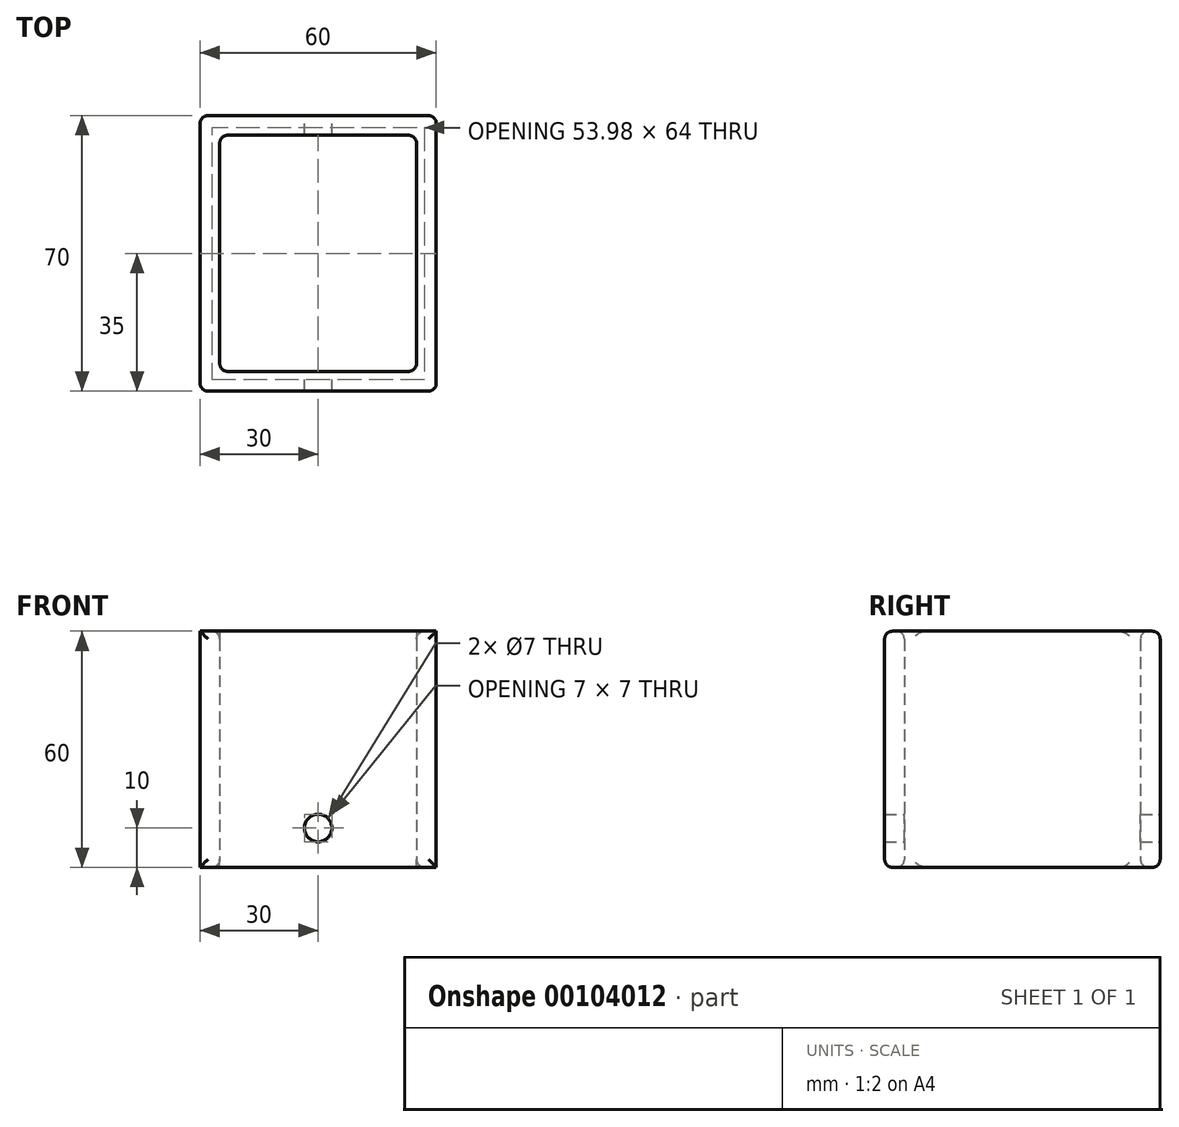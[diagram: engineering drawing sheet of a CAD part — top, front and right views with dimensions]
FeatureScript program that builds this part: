
annotation { "Feature Type Name" : "Feature", "Feature Type Description" : "" }
export const myFeature = defineFeature(function(context is Context, id is Id, definition is map)
    precondition{}
    {
        {
            var Q0;
            Q0=qCreatedBy(makeId("Top.planeOp"),FACE);
            var sketch = newSketch(context, id + "F0", { "sketchPlane" : qUnion([Q0])});
            skLineSegment(sketch, "E0.bottom", {"start": v(-30, 35) * mm, "end": v(30, 35) * mm});
            skLineSegment(sketch, "E0.top", {"start": v(-30, -35) * mm, "end": v(30, -35) * mm});
            skLineSegment(sketch, "E0.left", {"start": v(-30, 35) * mm, "end": v(-30, -35) * mm});
            skLineSegment(sketch, "E0.right", {"start": v(30, 35) * mm, "end": v(30, -35) * mm});
            skPoint(sketch, "E0.middle", {"position": v(0, 0) * mm});
            skLineSegment(sketch, "E1.bottom", {"start": v(25, 30) * mm, "end": v(-25, 30) * mm});
            skLineSegment(sketch, "E1.top", {"start": v(25, -30) * mm, "end": v(-25, -30) * mm});
            skLineSegment(sketch, "E1.left", {"start": v(25, 30) * mm, "end": v(25, -30) * mm});
            skLineSegment(sketch, "E1.right", {"start": v(-25, 30) * mm, "end": v(-25, -30) * mm});
            skSolve(sketch);
        }
        {
            var Q0;
            Q0=makeQuery(id+"F0.imprint","IMPRINT",FACE,{"disambiguationData":[TD([[makeQuery(id+"F0.imprint","IMPRINT",EDGE,{"derivedFrom":sQuery(id+"F0.wireOp",EDGE,"E0.bottom")}),-1.0]])]});
            extrude(context, id + "F1", {"entities" : qUnion([Q0]), "depth" : 60 * mm});
        }
        {
            var Q0;
            Q0=makeQuery(id+"F1.opExtrude","SWEPT_EDGE",EDGE,{"disambiguationData":[OSD([sQuery(id+"F0.wireOp",EDGE,"E0.bottom"),sQuery(id+"F0.wireOp",EDGE,"E0.left")])]});
            var Q1;
            Q1=makeQuery(id+"F1.opExtrude","CAP_EDGE",EDGE,{"disambiguationData":[OSD([sQuery(id+"F0.wireOp",EDGE,"E0.bottom")])],"isStart":false});
            var Q2;
            Q2=makeQuery(id+"F1.opExtrude","SWEPT_EDGE",EDGE,{"disambiguationData":[OSD([sQuery(id+"F0.wireOp",EDGE,"E0.bottom"),sQuery(id+"F0.wireOp",EDGE,"E0.right")])]});
            var Q3;
            Q3=makeQuery(id+"F1.opExtrude","CAP_EDGE",EDGE,{"disambiguationData":[OSD([sQuery(id+"F0.wireOp",EDGE,"E0.bottom")])],"isStart":true});
            var Q4;
            Q4=makeQuery(id+"F1.opExtrude","SWEPT_EDGE",EDGE,{"disambiguationData":[OSD([sQuery(id+"F0.wireOp",EDGE,"E0.top"),sQuery(id+"F0.wireOp",EDGE,"E0.right")])]});
            var Q5;
            Q5=makeQuery(id+"F1.opExtrude","CAP_EDGE",EDGE,{"disambiguationData":[OSD([sQuery(id+"F0.wireOp",EDGE,"E0.top")])],"isStart":false});
            var Q6;
            Q6=makeQuery(id+"F1.opExtrude","SWEPT_EDGE",EDGE,{"disambiguationData":[OSD([sQuery(id+"F0.wireOp",EDGE,"E0.top"),sQuery(id+"F0.wireOp",EDGE,"E0.left")])]});
            var Q7;
            Q7=makeQuery(id+"F1.opExtrude","CAP_EDGE",EDGE,{"disambiguationData":[OSD([sQuery(id+"F0.wireOp",EDGE,"E0.top")])],"isStart":true});
            var Q8;
            Q8=makeQuery(id+"F1.opExtrude","SWEPT_EDGE",EDGE,{"disambiguationData":[OSD([sQuery(id+"F0.wireOp",EDGE,"E1.top"),sQuery(id+"F0.wireOp",EDGE,"E1.right")])]});
            var Q9;
            Q9=makeQuery(id+"F1.opExtrude","CAP_EDGE",EDGE,{"disambiguationData":[OSD([sQuery(id+"F0.wireOp",EDGE,"E1.top")])],"isStart":false});
            var Q10;
            Q10=makeQuery(id+"F1.opExtrude","SWEPT_EDGE",EDGE,{"disambiguationData":[OSD([sQuery(id+"F0.wireOp",EDGE,"E1.top"),sQuery(id+"F0.wireOp",EDGE,"E1.left")])]});
            var Q11;
            Q11=makeQuery(id+"F1.opExtrude","CAP_EDGE",EDGE,{"disambiguationData":[OSD([sQuery(id+"F0.wireOp",EDGE,"E1.top")])],"isStart":true});
            var Q12;
            Q12=makeQuery(id+"F1.opExtrude","SWEPT_EDGE",EDGE,{"disambiguationData":[OSD([sQuery(id+"F0.wireOp",EDGE,"E1.bottom"),sQuery(id+"F0.wireOp",EDGE,"E1.left")])]});
            var Q13;
            Q13=makeQuery(id+"F1.opExtrude","CAP_EDGE",EDGE,{"disambiguationData":[OSD([sQuery(id+"F0.wireOp",EDGE,"E1.bottom")])],"isStart":false});
            var Q14;
            Q14=makeQuery(id+"F1.opExtrude","CAP_EDGE",EDGE,{"disambiguationData":[OSD([sQuery(id+"F0.wireOp",EDGE,"E1.bottom")])],"isStart":true});
            var Q15;
            Q15=makeQuery(id+"F1.opExtrude","SWEPT_FACE",FACE,{"disambiguationData":[OSD([sQuery(id+"F0.wireOp",EDGE,"E1.bottom")])]});
            fillet(context, id + "F2", {"entities" : qUnion([Q0, Q1, Q2, Q3, Q4, Q5, Q6, Q7, Q8, Q9, Q10, Q11, Q12, Q13, Q14, Q15]), "radius" : 2 * mm, "tangentPropagation" : true, "allowEdgeOverflow" : false});
        }
        {
            var Q0;
            Q0=makeQuery(id+"F1.opExtrude","SWEPT_FACE",FACE,{"disambiguationData":[OSD([sQuery(id+"F0.wireOp",EDGE,"E0.bottom")])]});
            var sketch = newSketch(context, id + "F3", { "sketchPlane" : qUnion([Q0])});
            skSolve(sketch);
        }
        {
            var Q0;
            {var subQ0=sQuery(id+"F0.wireOp",EDGE,"E0.bottom");var subQ1=makeQuery(id+"F1.opExtrude","SWEPT_FACE",FACE,{"disambiguationData":[OSD([subQ0])]});Q0=makeQuery(id+"F3.imprint","IMPRINT",FACE,{"disambiguationData":[TD([[makeQuery(id+"F3.imprint","IMPRINT",EDGE,{"derivedFrom":makeQuery(id+"F2.opFillet","BLEND_EDGE",EDGE,{"blendedFrom":[makeQuery(id+"F1.opExtrude","CAP_EDGE",EDGE,{"disambiguationData":[OSD([subQ0])],"isStart":true}),subQ1],"blendedInto":[subQ1]})}),1.0]])]});}
            var sketch = newSketch(context, id + "F4", { "sketchPlane" : qUnion([Q0])});
            skCircle(sketch, "E2", {"center": v(0, 10) * mm, "radius": 3.5 * mm});
            skSolve(sketch);
        }
        {
            var Q0;
            Q0 = qSketchRegion(id + "F4", true);
            extrude(context, id + "F5", {"entities" : qUnion([Q0]), "operationType" : NewBodyOperationType.REMOVE, "oppositeDirection" : true, "depth" : 70 * mm});
        }
    });
